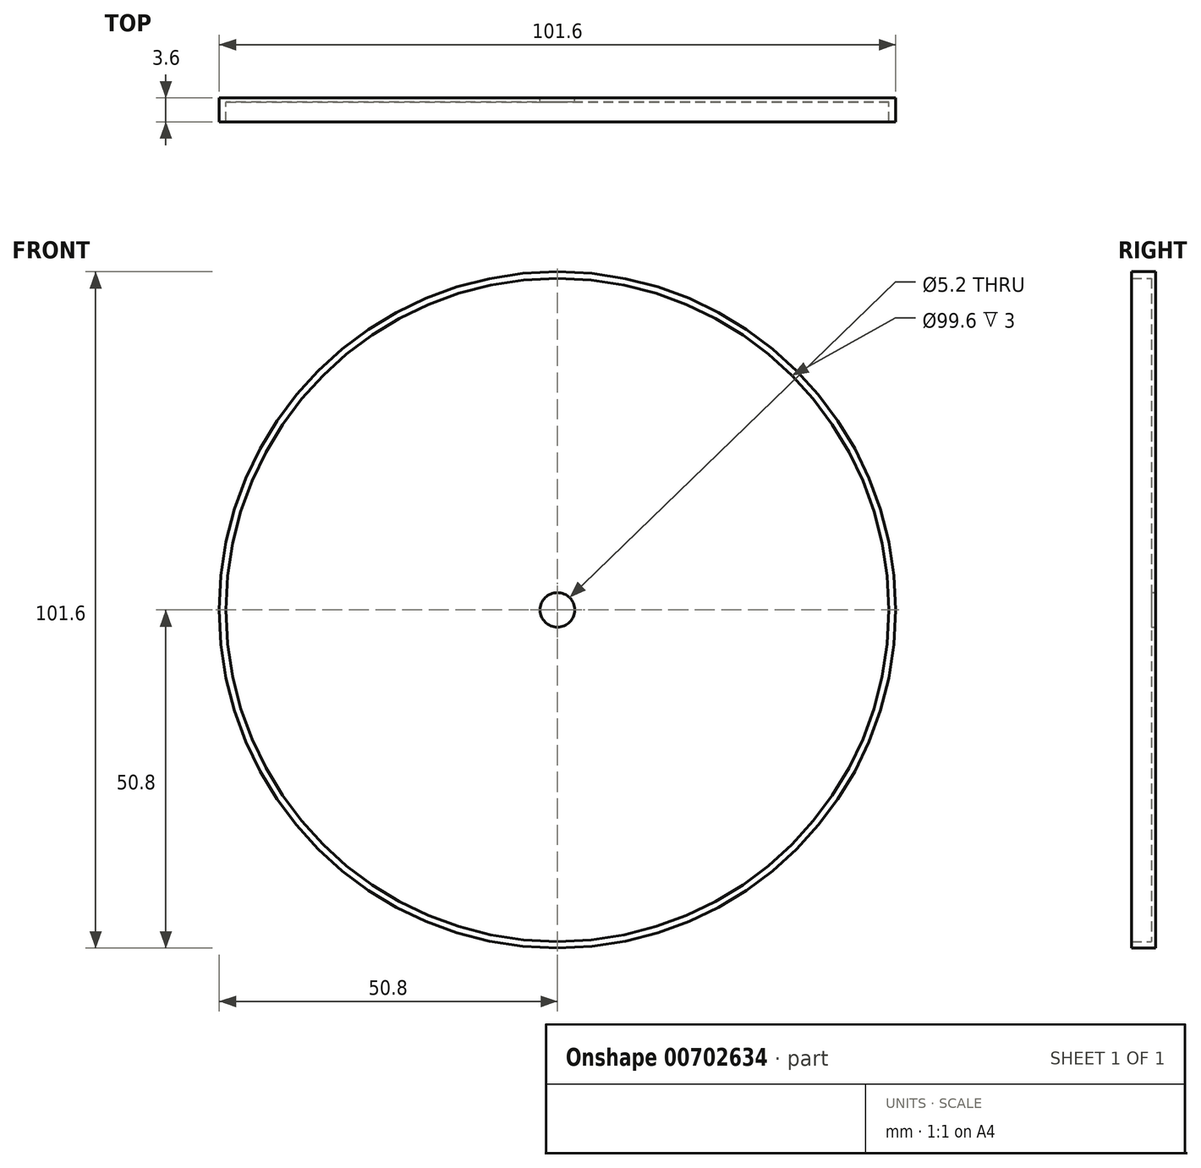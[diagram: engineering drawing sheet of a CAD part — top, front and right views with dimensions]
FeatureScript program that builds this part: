
annotation { "Feature Type Name" : "Feature", "Feature Type Description" : "" }
export const myFeature = defineFeature(function(context is Context, id is Id, definition is map)
    precondition{}
    {
        {
            var Q0;
            Q0=qCreatedBy(makeId("Top.planeOp"),FACE);
            var sketch = newSketch(context, id + "F0", { "sketchPlane" : qUnion([Q0])});
            skLineSegment(sketch, "E0", {"start": v(-2.6, 0) * mm, "end": v(-50.8, 0) * mm});
            skLineSegment(sketch, "E1", {"start": v(-50.8, 0) * mm, "end": v(-50.8, -3.6) * mm});
            skLineSegment(sketch, "E2", {"start": v(-50.8, -3.6) * mm, "end": v(-49.8, -3.6) * mm});
            skLineSegment(sketch, "E3", {"start": v(-49.8, -3.6) * mm, "end": v(-49.8, -0.6) * mm});
            skLineSegment(sketch, "E4", {"start": v(-49.8, -0.6) * mm, "end": v(-2.6, -0.6) * mm});
            skLineSegment(sketch, "E5", {"start": v(-2.6, -0.6) * mm, "end": v(-2.6, 0) * mm});
            skLineSegment(sketch, "E6", {"start": v(-2.6, 0) * mm, "end": v(0, 0) * mm, "construction": true});
            skLineSegment(sketch, "E7", {"start": v(0, 0) * mm, "end": v(0, -3.3) * mm, "construction": true});
            skSolve(sketch);
        }
        {
            var Q0;
            Q0 = qSketchRegion(id + "F0", true);
            var Q1;
            Q1=sQuery(id+"F0.wireOp",EDGE,"E7");
            revolve(context, id + "F1", {"surfaceOperationType" : NewSurfaceOperationType.NEW, "entities" : qUnion([Q0]), "axis" : qUnion([Q1]), "revolveType" : RevolveType.FULL});
        }
    });
